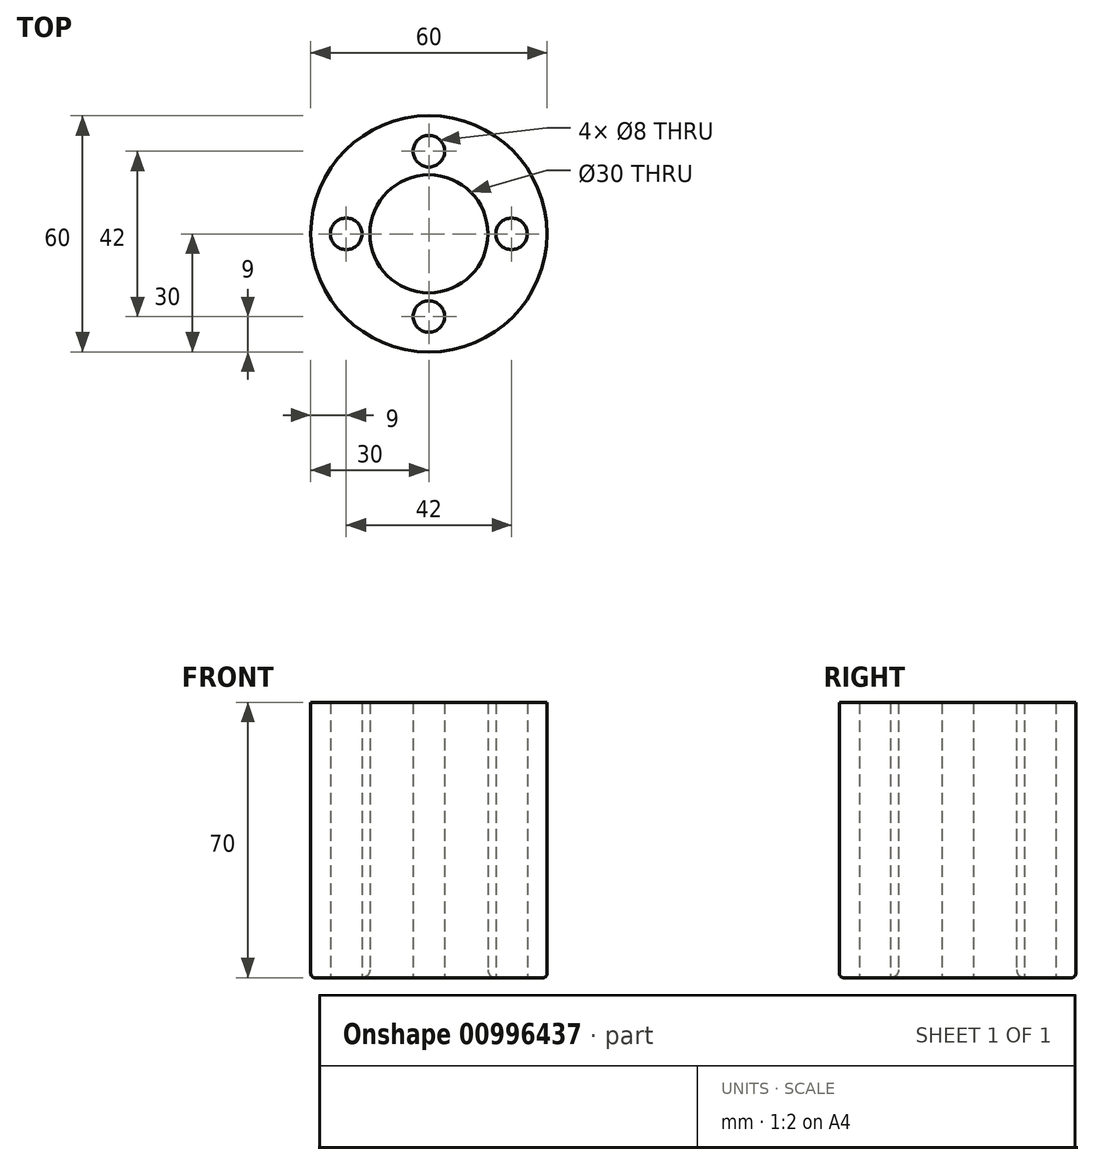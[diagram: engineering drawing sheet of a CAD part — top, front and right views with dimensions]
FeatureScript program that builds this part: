
annotation { "Feature Type Name" : "Feature", "Feature Type Description" : "" }
export const myFeature = defineFeature(function(context is Context, id is Id, definition is map)
    precondition{}
    {
        {
            var Q0;
            Q0=qCreatedBy(makeId("Top.planeOp"),FACE);
            var sketch = newSketch(context, id + "F0", { "sketchPlane" : qUnion([Q0])});
            skCircle(sketch, "E0", {"center": v(0, 0) * mm, "radius": 15 * mm});
            skCircle(sketch, "E1", {"center": v(0, 0) * mm, "radius": 30 * mm});
            skCircle(sketch, "E2", {"center": v(0, 0) * mm, "radius": 21 * mm, "construction": true});
            skCircle(sketch, "E3", {"center": v(0, 21) * mm, "radius": 4 * mm});
            skCircle(sketch, "E4.MirrorC", {"center": v(0, -21) * mm, "radius": 4 * mm});
            skCircle(sketch, "E5", {"center": v(-21, 0) * mm, "radius": 4 * mm});
            skCircle(sketch, "E6.MirrorC", {"center": v(21, 0) * mm, "radius": 4 * mm});
            skSolve(sketch);
        }
        {
            var Q0;
            Q0=makeQuery(id+"F0.imprint","IMPRINT",FACE,{"disambiguationData":[TD([[makeQuery(id+"F0.imprint","IMPRINT",EDGE,{"derivedFrom":sQuery(id+"F0.wireOp",EDGE,"E0")}),-1.0]])]});
            extrude(context, id + "F1", {"entities" : qUnion([Q0]), "depth" : 70 * mm, "offsetDistance" : 25 * mm});
        }
        {
            var Q0;
            Q0=makeQuery(id+"F1.opExtrude","CAP_EDGE",EDGE,{"disambiguationData":[OSD([sQuery(id+"F0.wireOp",EDGE,"E0")])],"isStart":true});
            fillet(context, id + "F2", {"entities" : qUnion([Q0]), "radius" : 2 * mm, "tangentPropagation" : true, "allowEdgeOverflow" : false});
        }
        {
            var Q0;
            Q0=makeQuery(id+"F1.opExtrude","CAP_EDGE",EDGE,{"disambiguationData":[OSD([sQuery(id+"F0.wireOp",EDGE,"E1")])],"isStart":true});
            fillet(context, id + "F3", {"entities" : qUnion([Q0]), "radius" : 1 * mm, "tangentPropagation" : true, "allowEdgeOverflow" : false});
        }
    });
